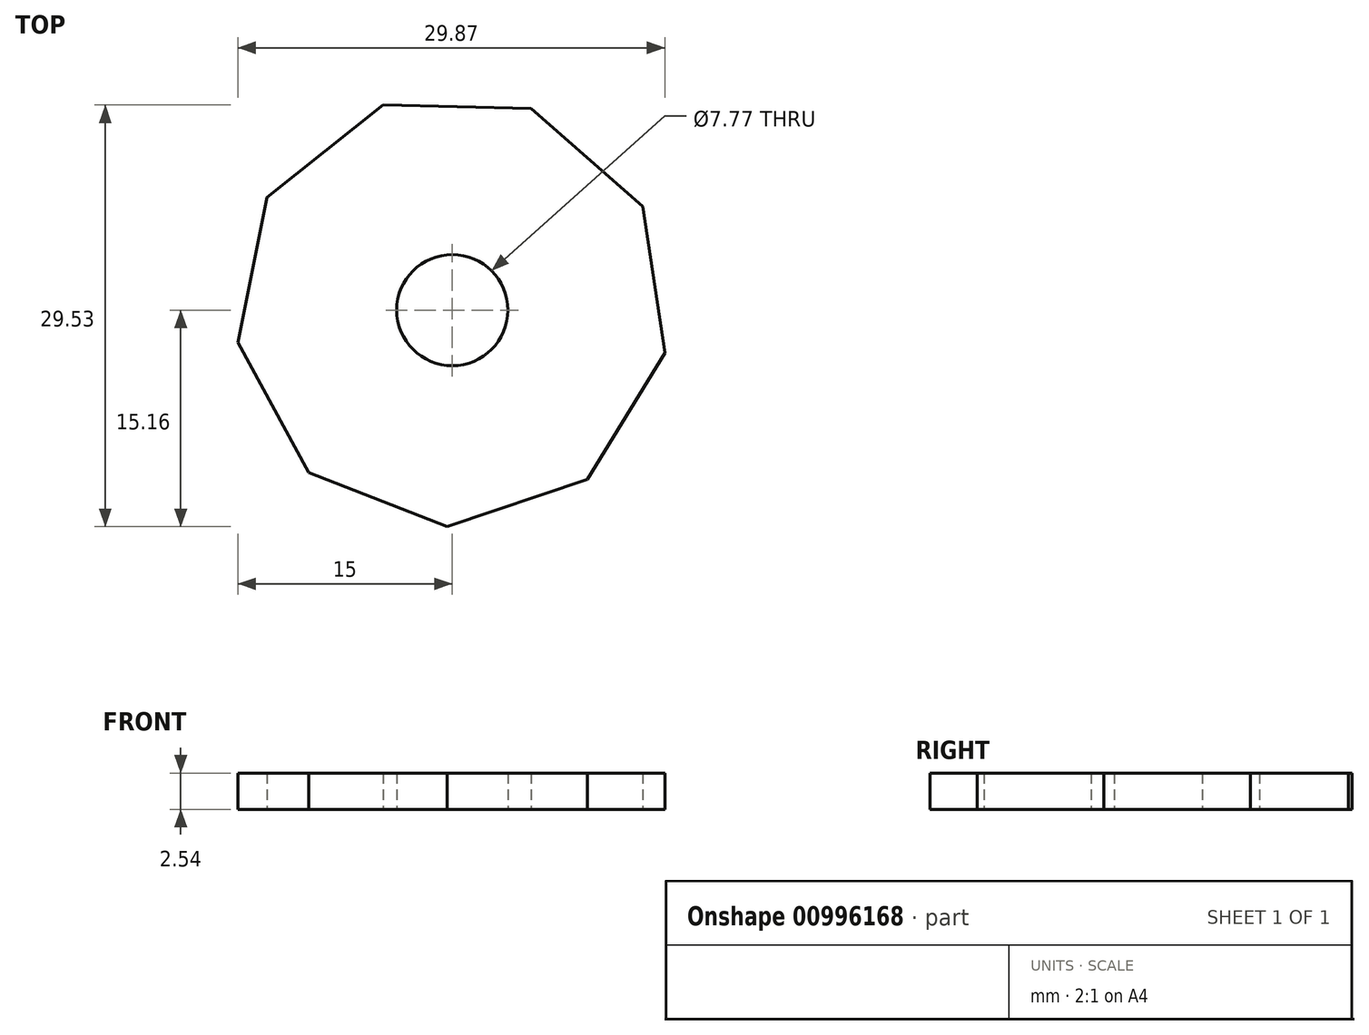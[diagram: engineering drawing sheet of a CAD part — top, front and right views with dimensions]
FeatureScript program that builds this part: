
annotation { "Feature Type Name" : "Feature", "Feature Type Description" : "" }
export const myFeature = defineFeature(function(context is Context, id is Id, definition is map)
    precondition{}
    {
        {
            var Q0;
            Q0=qCreatedBy(makeId("Top.planeOp"),FACE);
            var sketch = newSketch(context, id + "F0", { "sketchPlane" : qUnion([Q0])});
            skCircle(sketch, "E0.cCircle", {"center": v(0, 0) * mm, "radius": 14.25 * mm, "construction": true});
            skLineSegment(sketch, "E0.0", {"start": v(9.47, -11.85) * mm, "end": v(-0.36, -15.16) * mm});
            skLineSegment(sketch, "E0.1", {"start": v(-0.36, -15.16) * mm, "end": v(-10.03, -11.38) * mm});
            skLineSegment(sketch, "E0.2", {"start": v(-10.03, -11.38) * mm, "end": v(-15, -2.27) * mm});
            skLineSegment(sketch, "E0.3", {"start": v(-15, -2.27) * mm, "end": v(-12.95, 7.9) * mm});
            skLineSegment(sketch, "E0.4", {"start": v(-12.95, 7.9) * mm, "end": v(-4.84, 14.37) * mm});
            skLineSegment(sketch, "E0.5", {"start": v(-4.84, 14.37) * mm, "end": v(5.53, 14.12) * mm});
            skLineSegment(sketch, "E0.6", {"start": v(5.53, 14.12) * mm, "end": v(13.31, 7.27) * mm});
            skLineSegment(sketch, "E0.7", {"start": v(13.31, 7.27) * mm, "end": v(14.87, -3) * mm});
            skLineSegment(sketch, "E0.8", {"start": v(14.87, -3) * mm, "end": v(9.47, -11.85) * mm});
            skPoint(sketch, "E0.0.midPoint", {"position": v(4.55, -13.5) * mm});
            skCircle(sketch, "E1", {"center": v(0, 0) * mm, "radius": 3.89 * mm});
            skSolve(sketch);
        }
        {
            var Q0;
            Q0=makeQuery(id+"F0.imprint","IMPRINT",FACE,{"disambiguationData":[TD([[makeQuery(id+"F0.imprint","IMPRINT",EDGE,{"derivedFrom":sQuery(id+"F0.wireOp",EDGE,"E0.0")}),-1.0]])]});
            extrude(context, id + "F1", {"entities" : qUnion([Q0]), "depth" : 2.54 * mm, "offsetDistance" : 25.4 * mm});
        }
    });
